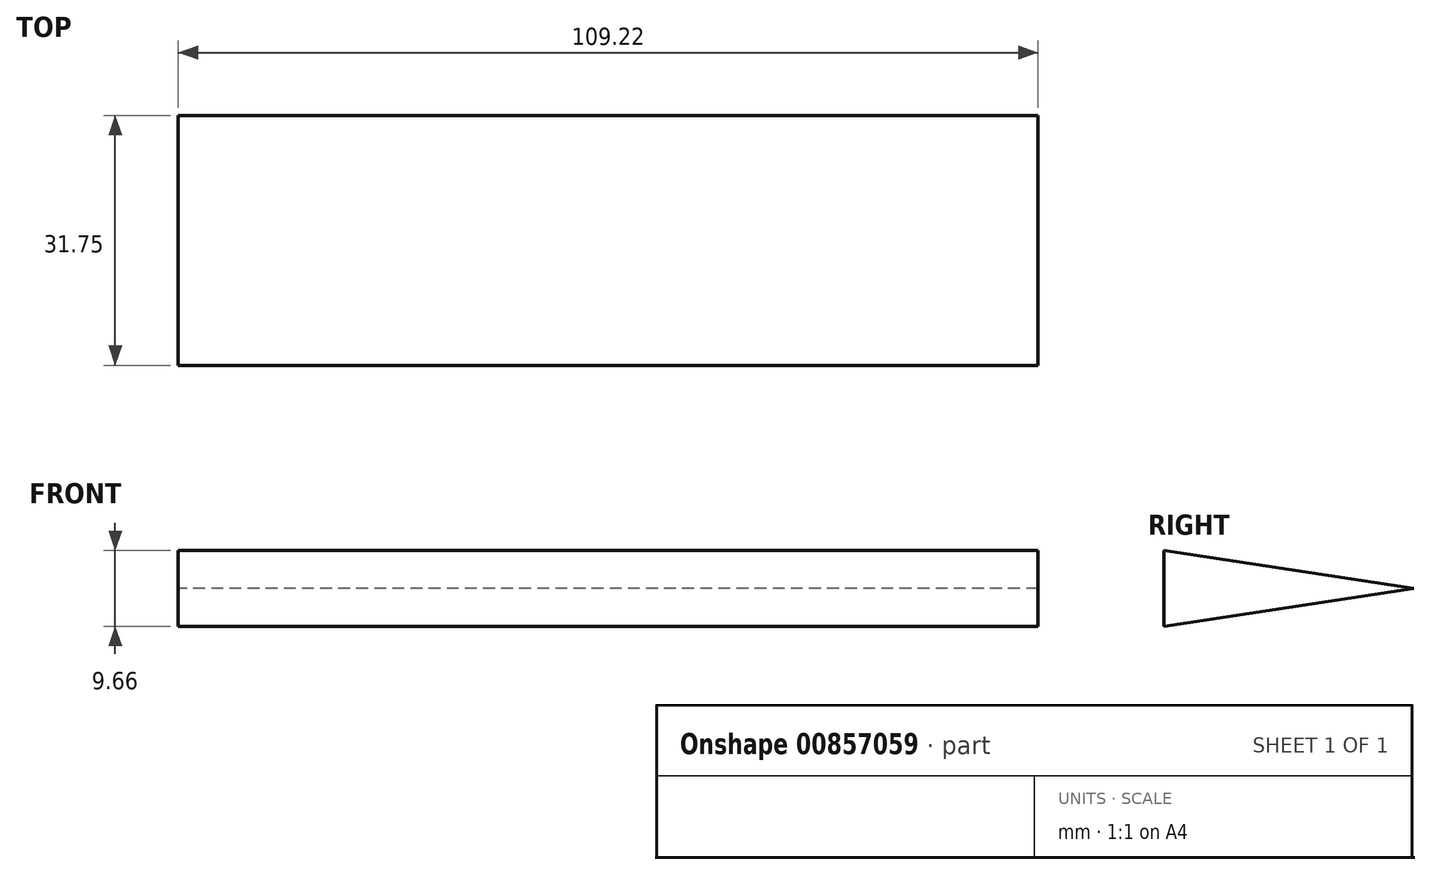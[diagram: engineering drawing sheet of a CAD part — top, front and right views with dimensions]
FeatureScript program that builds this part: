
annotation { "Feature Type Name" : "Feature", "Feature Type Description" : "" }
export const myFeature = defineFeature(function(context is Context, id is Id, definition is map)
    precondition{}
    {
        {
            var Q0;
            Q0=qCreatedBy(makeId("Right.planeOp"),FACE);
            var sketch = newSketch(context, id + "F0", { "sketchPlane" : qUnion([Q0])});
            skLineSegment(sketch, "E0", {"start": v(0, 48.82) * mm, "end": v(0, -48.82) * mm});
            skLineSegment(sketch, "E1", {"start": v(257.19, 9.65) * mm, "end": v(257.19, -9.65) * mm});
            skCircle(sketch, "E2", {"center": v(311.35, 0) * mm, "radius": 1.39 * mm});
            skLineSegment(sketch, "E3", {"start": v(0, 48.82) * mm, "end": v(311.56, 1.37) * mm});
            skLineSegment(sketch, "E4", {"start": v(0, -48.82) * mm, "end": v(311.56, -1.37) * mm});
            skLineSegment(sketch, "E5", {"start": v(257.19, 4.83) * mm, "end": v(288.94, 0) * mm});
            skLineSegment(sketch, "E6", {"start": v(288.94, 0) * mm, "end": v(257.19, -4.83) * mm});
            skSolve(sketch);
        }
        {
            var Q0;
            {var subQ0=sQuery(id+"F0.wireOp",EDGE,"E5");Q0=makeQuery(id+"F0.imprint","IMPRINT",FACE,{"disambiguationData":[TD([[makeQuery(id+"F0.imprint","IMPRINT",EDGE,{"derivedFrom":subQ0}),-1.0]])]});}
            extrude(context, id + "F1", {"entities" : qUnion([Q0]), "depth" : 109.22 * mm, "offsetDistance" : 25.4 * mm, "symmetric" : true});
        }
    });
